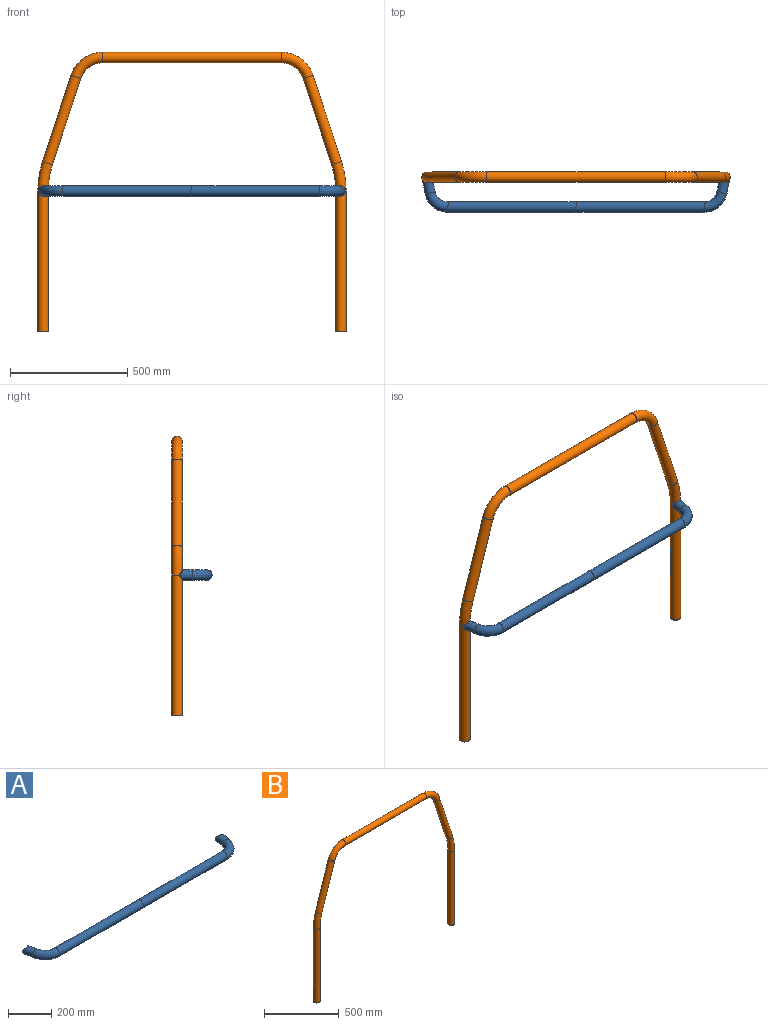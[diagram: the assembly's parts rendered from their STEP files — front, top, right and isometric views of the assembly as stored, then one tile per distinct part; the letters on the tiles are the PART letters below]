
ASSEMBLY  parts=2 mates=1
PART A: 14 faces, bbox 1329.2x183.4x44.5 mm
  f0: bspline ~57.82x49.58mm, area 5932.8mm2, adj f1,f7
  f1: bspline ~120.6x98.87mm, area 12517.8mm2, adj f0,f2
  f2: bspline ~562.17x75.22mm, area 65411.3mm2, adj f1,f3
  f3: bspline ~562.17x75.22mm, area 65411.3mm2, adj f2,f4
  f4: bspline ~117.65x117.36mm, area 12517.8mm2, adj f3,f5
  f5: bspline ~72.44x46.65mm, area 5933.2mm2, adj f4,f6
  f6: cylinder r=22.23mm len=44.45mm, axis (0,0,1), area 599.4mm2, adj f5,f10
  f7: cylinder r=22.23mm len=44.45mm, axis (0,0,1), area 597.7mm2, adj f0,f13
  f8: bspline ~564.57x87.17mm, area 75807.8mm2, adj f9,f11
  f9: bspline ~126.28x124.47mm, area 14509.9mm2, adj f8,f10
  f10: bspline ~82.69x53.82mm, area 7234.4mm2, adj f6,f9
  f11: bspline ~564.57x87.17mm, area 75807.8mm2, adj f8,f12
  f12: bspline ~127.89x104.84mm, area 14509.9mm2, adj f11,f13
  f13: bspline ~65.74x57.21mm, area 7237.2mm2, adj f7,f12
PART B: 20 faces, bbox 1324.7x44.5x1202.4 mm
  f0: cylinder r=19.18mm len=599.42mm, axis (0,0,1), area 72225.7mm2, adj f1,f9
  f1: torus R=381mm, axis (0,1,0), area 14571.7mm2, adj f0,f2
  f2: cylinder r=19.18mm len=379.28mm, axis (0.31,0,0.95), area 46584.8mm2, adj f1,f3
  f3: torus R=120.31mm, axis (0,1,0), area 18169.6mm2, adj f2,f4
  f4: cylinder r=19.18mm len=762mm, axis (1,0,0), area 91815.4mm2, adj f3,f5
  f5: torus R=120.31mm, axis (0,1,0), area 18169.6mm2, adj f4,f6
  f6: cylinder r=19.18mm len=379.28mm, axis (0.31,0,-0.95), area 46584.8mm2, adj f5,f7
  f7: torus R=381mm, axis (0,1,0), area 14571.7mm2, adj f6,f8
  f8: cylinder r=19.18mm len=599.42mm, axis (0,0,-1), area 72225.7mm2, adj f7,f10
  f9: plane 44.45x44.45mm, normal (0,0,-1), area 396.4mm2, adj f0,f11
  f10: plane 44.45x44.45mm, normal (0,0,-1), area 396.4mm2, adj f8,f19
  f11: cylinder r=22.23mm len=599.42mm, axis (0,0,1), area 83705.3mm2, adj f9,f12
  f12: torus R=381mm, axis (0,1,0), area 16887.7mm2, adj f11,f13
  f13: cylinder r=22.23mm len=381.18mm, axis (0.31,0,0.95), area 53989mm2, adj f12,f14
  f14: torus R=120.31mm, axis (0,1,0), area 21057.5mm2, adj f13,f15
  f15: cylinder r=22.23mm len=762mm, axis (1,0,0), area 106408.6mm2, adj f14,f16
  f16: torus R=120.31mm, axis (0,1,0), area 21057.5mm2, adj f15,f17
  f17: cylinder r=22.23mm len=381.18mm, axis (0.31,0,-0.95), area 53989mm2, adj f16,f18
  f18: torus R=381mm, axis (0,1,0), area 16887.7mm2, adj f17,f19
  f19: cylinder r=22.23mm len=599.42mm, axis (0,0,-1), area 83705.3mm2, adj f10,f18
PLACE A rot(axis=(-0.24,-0.93,0.27),0deg) t=(-245.69,302.27,707.28)mm
PLACE B rot(axis=(-0.24,-0.93,0.27),0deg) t=(-245.69,302.27,107.89)mm
MATE slider A.f6 <-> B.f19  axis (0,0,1) through (389.31,302.27,707.31)mm
